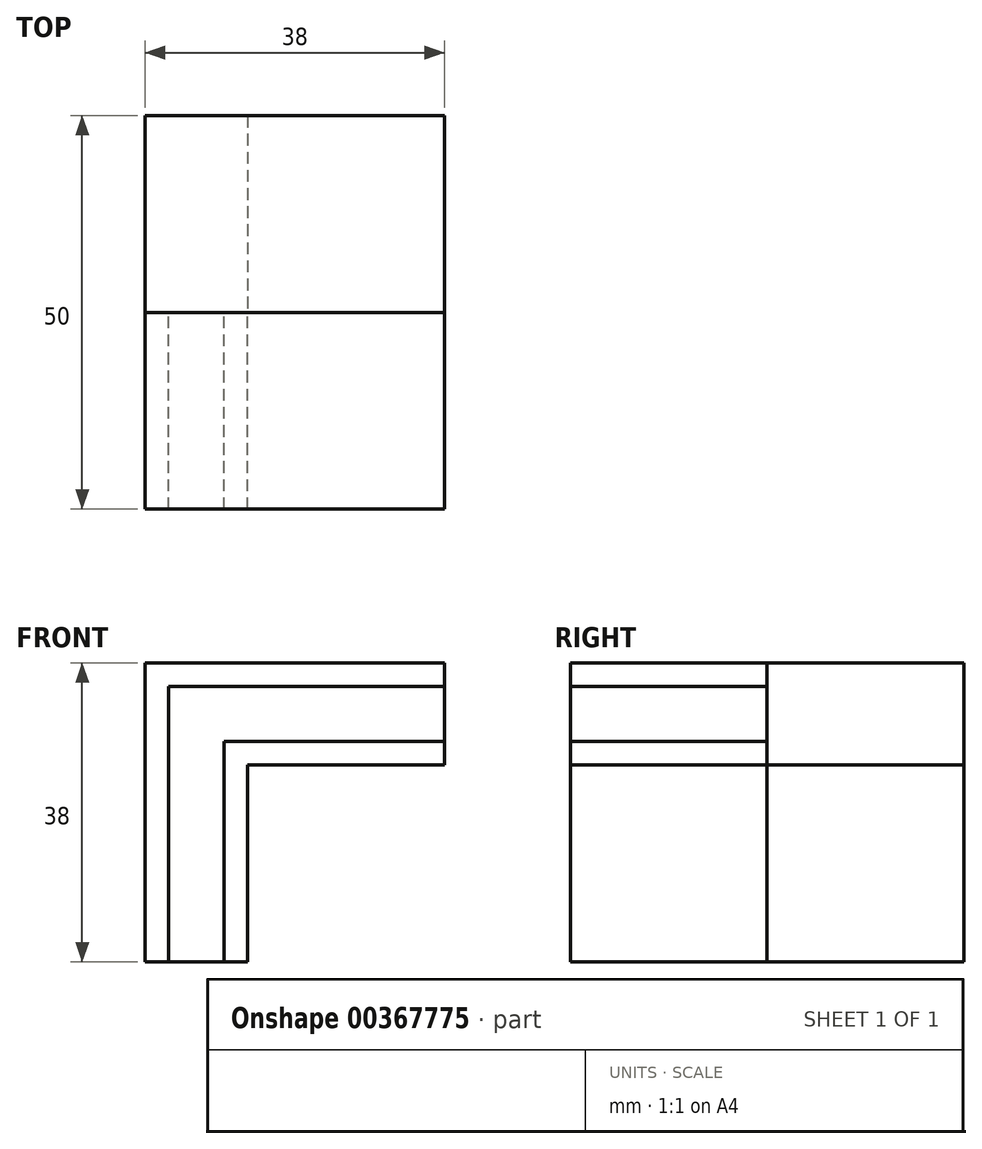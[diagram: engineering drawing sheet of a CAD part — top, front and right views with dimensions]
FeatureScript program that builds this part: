
annotation { "Feature Type Name" : "Feature", "Feature Type Description" : "" }
export const myFeature = defineFeature(function(context is Context, id is Id, definition is map)
    precondition{}
    {
        {
            var Q0;
            Q0=qCreatedBy(makeId("Front.planeOp"),FACE);
            var sketch = newSketch(context, id + "F0", { "sketchPlane" : qUnion([Q0])});
            skLineSegment(sketch, "E0.top", {"start": v(0, -25) * mm, "end": v(-13, -25) * mm});
            skLineSegment(sketch, "E0.left", {"start": v(0, 0) * mm, "end": v(0, -25) * mm});
            skLineSegment(sketch, "E0.right", {"start": v(-13, 0) * mm, "end": v(-13, -25) * mm});
            skLineSegment(sketch, "E1.top", {"start": v(7, 13) * mm, "end": v(-13, 13) * mm});
            skLineSegment(sketch, "E1.right", {"start": v(-13, 0) * mm, "end": v(-13, 13) * mm});
            skLineSegment(sketch, "E2.bottom", {"start": v(0, 0) * mm, "end": v(25, 0) * mm});
            skLineSegment(sketch, "E2.top", {"start": v(7, 13) * mm, "end": v(25, 13) * mm});
            skLineSegment(sketch, "E2.right", {"start": v(25, 0) * mm, "end": v(25, 13) * mm});
            skLineSegment(sketch, "E3.0", {"start": v(-3, 3) * mm, "end": v(25, 3) * mm});
            skLineSegment(sketch, "E3.1", {"start": v(-3, 3) * mm, "end": v(-3, -25.05) * mm});
            skLineSegment(sketch, "E4.0", {"start": v(-10, 0) * mm, "end": v(-10, -25.05) * mm});
            skLineSegment(sketch, "E4.1", {"start": v(-10, 0) * mm, "end": v(-10, 10) * mm});
            skLineSegment(sketch, "E4.2", {"start": v(7, 10) * mm, "end": v(-10, 10) * mm});
            skLineSegment(sketch, "E4.3", {"start": v(7, 10) * mm, "end": v(25, 10) * mm});
            skSolve(sketch);
        }
        {
            var Q0;
            {var subQ1=sQuery(id+"F0.wireOp",EDGE,"E0.right");Q0=makeQuery(id+"F0.imprint","IMPRINT",FACE,{"disambiguationData":[TD([[makeQuery(id+"F0.imprint","IMPRINT",EDGE,{"derivedFrom":subQ1}),1.0]])]});}
            var Q1;
            {var subQ3=sQuery(id+"F0.wireOp",EDGE,"E0.left");Q1=makeQuery(id+"F0.imprint","IMPRINT",FACE,{"disambiguationData":[TD([[makeQuery(id+"F0.imprint","IMPRINT",EDGE,{"derivedFrom":subQ3}),-1.0]])]});}
            extrude(context, id + "F1", {"entities" : qUnion([Q0, Q1]), "depth" : 25 * mm});
        }
        {
            var Q0;
            Q0 = qSketchRegion(id + "F0", true);
            extrude(context, id + "F2", {"entities" : qUnion([Q0]), "oppositeDirection" : true, "depth" : 25 * mm});
        }
    });
